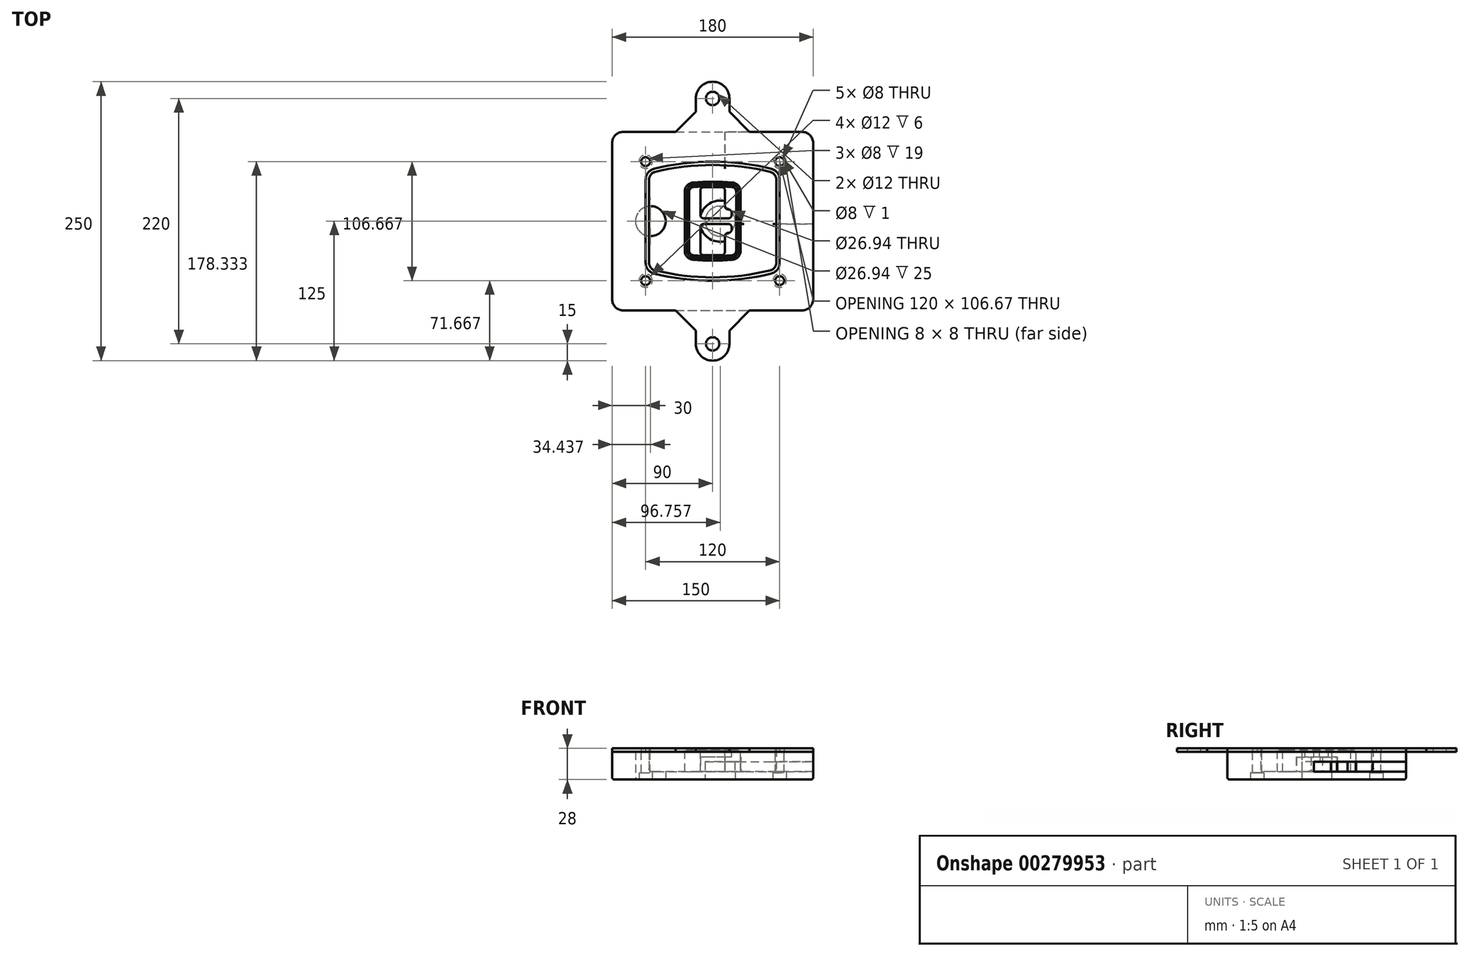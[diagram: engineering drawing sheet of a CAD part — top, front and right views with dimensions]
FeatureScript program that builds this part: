
annotation { "Feature Type Name" : "Feature", "Feature Type Description" : "" }
export const myFeature = defineFeature(function(context is Context, id is Id, definition is map)
    precondition{}
    {
        {
            var Q0;
            Q0=qCreatedBy(makeId("Top.planeOp"),FACE);
            var sketch = newSketch(context, id + "F0", { "sketchPlane" : qUnion([Q0])});
            skPoint(sketch, "E0.rect.middle", {"position": v(0, 0) * mm});
            skLineSegment(sketch, "E1.bottom", {"start": v(-80, -80) * mm, "end": v(80, -80) * mm});
            skLineSegment(sketch, "E1.top", {"start": v(-80, 80) * mm, "end": v(80, 80) * mm});
            skLineSegment(sketch, "E1.left", {"start": v(-90, -70) * mm, "end": v(-90, 70) * mm});
            skLineSegment(sketch, "E1.right", {"start": v(90, -70) * mm, "end": v(90, 70) * mm});
            skLineSegment(sketch, "E2", {"start": v(-90, 80) * mm, "end": v(90, -80) * mm, "construction": true});
            skLineSegment(sketch, "E3", {"start": v(90, 80) * mm, "end": v(-90, -80) * mm, "construction": true});
            skCircle(sketch, "E4", {"center": v(-60, 53.33) * mm, "radius": 4 * mm});
            skCircle(sketch, "E5", {"center": v(60, 53.33) * mm, "radius": 4 * mm});
            skCircle(sketch, "E6", {"center": v(60, -53.33) * mm, "radius": 4 * mm});
            skCircle(sketch, "E7", {"center": v(-60, -53.33) * mm, "radius": 4 * mm});
            skLineSegment(sketch, "E8", {"start": v(-60, 53.33) * mm, "end": v(60, 53.33) * mm, "construction": true});
            skLineSegment(sketch, "E9", {"start": v(60, 53.33) * mm, "end": v(60, -53.33) * mm, "construction": true});
            skLineSegment(sketch, "E10", {"start": v(60, -53.33) * mm, "end": v(-60, -53.33) * mm, "construction": true});
            skLineSegment(sketch, "E11", {"start": v(-60, -53.33) * mm, "end": v(-60, 53.33) * mm, "construction": true});
            skLineSegment(sketch, "E12", {"start": v(-60, 37.3) * mm, "end": v(-60, -37.3) * mm});
            skLineSegment(sketch, "E13", {"start": v(60, 37.3) * mm, "end": v(60, -37.3) * mm});
            skArc(sketch, "E14", {"start": v(52.38, 47.01) * mm, "mid": v(0, 53.33) * mm, "end": v(-52.38, 47.01) * mm});
            skArc(sketch, "E15", {"start": v(-52.38, -47.01) * mm, "mid": v(0, -53.33) * mm, "end": v(52.38, -47.01) * mm});
            skLineSegment(sketch, "E16", {"start": v(-60, 0) * mm, "end": v(60, 0) * mm, "construction": true});
            skPoint(sketch, "E17.visualSharp", {"position": v(-60, -45) * mm});
            skArc(sketch, "E17.filletArc", {"start": v(-60, -37.3) * mm, "mid": v(-57.87, -43.47) * mm, "end": v(-52.38, -47.01) * mm});
            skPoint(sketch, "E18.visualSharp", {"position": v(-60, 45) * mm});
            skArc(sketch, "E18.filletArc", {"start": v(-52.38, 47.01) * mm, "mid": v(-57.87, 43.47) * mm, "end": v(-60, 37.3) * mm});
            skPoint(sketch, "E19.visualSharp", {"position": v(60, 45) * mm});
            skArc(sketch, "E19.filletArc", {"start": v(60, 37.3) * mm, "mid": v(57.87, 43.47) * mm, "end": v(52.38, 47.01) * mm});
            skPoint(sketch, "E20.visualSharp", {"position": v(60, -45) * mm});
            skArc(sketch, "E20.filletArc", {"start": v(52.38, -47.01) * mm, "mid": v(57.87, -43.47) * mm, "end": v(60, -37.3) * mm});
            skPoint(sketch, "E21.visualSharp", {"position": v(-90, 80) * mm});
            skArc(sketch, "E21.filletArc", {"start": v(-80, 80) * mm, "mid": v(-87.07, 77.07) * mm, "end": v(-90, 70) * mm});
            skPoint(sketch, "E22.visualSharp", {"position": v(90, 80) * mm});
            skArc(sketch, "E22.filletArc", {"start": v(90, 70) * mm, "mid": v(87.07, 77.07) * mm, "end": v(80, 80) * mm});
            skPoint(sketch, "E23.visualSharp", {"position": v(90, -80) * mm});
            skArc(sketch, "E23.filletArc", {"start": v(80, -80) * mm, "mid": v(87.07, -77.07) * mm, "end": v(90, -70) * mm});
            skPoint(sketch, "E24.visualSharp", {"position": v(-90, -80) * mm});
            skArc(sketch, "E24.filletArc", {"start": v(-90, -70) * mm, "mid": v(-87.07, -77.07) * mm, "end": v(-80, -80) * mm});
            skArc(sketch, "E25.0", {"start": v(57, 37.3) * mm, "mid": v(55.5, 41.62) * mm, "end": v(51.67, 44.1) * mm});
            skLineSegment(sketch, "E25.1", {"start": v(57, 37.3) * mm, "end": v(57, -37.3) * mm});
            skArc(sketch, "E25.2", {"start": v(51.67, -44.1) * mm, "mid": v(55.5, -41.62) * mm, "end": v(57, -37.3) * mm});
            skArc(sketch, "E25.3", {"start": v(-51.67, -44.1) * mm, "mid": v(0, -50.33) * mm, "end": v(51.67, -44.1) * mm});
            skArc(sketch, "E25.4", {"start": v(-57, -37.3) * mm, "mid": v(-55.5, -41.62) * mm, "end": v(-51.67, -44.1) * mm});
            skArc(sketch, "E25.5", {"start": v(51.67, 44.1) * mm, "mid": v(0, 50.33) * mm, "end": v(-51.67, 44.1) * mm});
            skLineSegment(sketch, "E25.6", {"start": v(-57, 37.3) * mm, "end": v(-57, -37.3) * mm});
            skArc(sketch, "E25.7", {"start": v(-51.67, 44.1) * mm, "mid": v(-55.5, 41.62) * mm, "end": v(-57, 37.3) * mm});
            skArc(sketch, "E26.0", {"start": v(-53.33, 50.9) * mm, "mid": v(-61.01, 45.94) * mm, "end": v(-64, 37.3) * mm});
            skArc(sketch, "E26.1", {"start": v(53.33, 50.9) * mm, "mid": v(0, 57.33) * mm, "end": v(-53.33, 50.9) * mm});
            skArc(sketch, "E26.2", {"start": v(64, 37.3) * mm, "mid": v(61.01, 45.94) * mm, "end": v(53.33, 50.9) * mm});
            skLineSegment(sketch, "E26.3", {"start": v(64, 37.3) * mm, "end": v(64, -37.3) * mm});
            skArc(sketch, "E26.4", {"start": v(53.33, -50.9) * mm, "mid": v(61.01, -45.94) * mm, "end": v(64, -37.3) * mm});
            skLineSegment(sketch, "E26.5", {"start": v(-64, 37.3) * mm, "end": v(-64, -37.3) * mm});
            skArc(sketch, "E26.6", {"start": v(-53.33, -50.9) * mm, "mid": v(0, -57.33) * mm, "end": v(53.33, -50.9) * mm});
            skArc(sketch, "E26.7", {"start": v(-64, -37.3) * mm, "mid": v(-61.01, -45.94) * mm, "end": v(-53.33, -50.9) * mm});
            skSolve(sketch);
        }
        {
            var Q0;
            Q0=makeQuery(id+"F0.imprint","IMPRINT",FACE,{"disambiguationData":[TD([[makeQuery(id+"F0.imprint","IMPRINT",EDGE,{"derivedFrom":sQuery(id+"F0.wireOp",EDGE,"E1.bottom")}),1.0]])]});
            var Q1;
            Q1=makeQuery(id+"F0.imprint","IMPRINT",FACE,{"disambiguationData":[TD([[makeQuery(id+"F0.imprint","IMPRINT",EDGE,{"derivedFrom":sQuery(id+"F0.wireOp",EDGE,"E12")}),1.0]])]});
            var Q2;
            Q2=makeQuery(id+"F0.imprint","IMPRINT",FACE,{"disambiguationData":[TD([[makeQuery(id+"F0.imprint","IMPRINT",EDGE,{"derivedFrom":sQuery(id+"F0.wireOp",EDGE,"E25.0")}),1.0]])]});
            var Q3;
            Q3=makeQuery(id+"F0.imprint","IMPRINT",FACE,{"disambiguationData":[TD([[makeQuery(id+"F0.imprint","IMPRINT",EDGE,{"derivedFrom":sQuery(id+"F0.wireOp",EDGE,"E12")}),-1.0]])]});
            extrude(context, id + "F1", {"entities" : qUnion([Q0, Q1, Q2, Q3]), "oppositeDirection" : true, "depth" : 25 * mm});
        }
        {
            var Q0;
            Q0=makeQuery(id+"F0.imprint","IMPRINT",FACE,{"disambiguationData":[TD([[makeQuery(id+"F0.imprint","IMPRINT",EDGE,{"derivedFrom":sQuery(id+"F0.wireOp",EDGE,"E12")}),1.0]])]});
            extrude(context, id + "F2", {"entities" : qUnion([Q0]), "operationType" : NewBodyOperationType.ADD, "depth" : 3 * mm});
        }
        {
            var Q0;
            Q0=makeQuery(id+"F0.imprint","IMPRINT",FACE,{"disambiguationData":[TD([[makeQuery(id+"F0.imprint","IMPRINT",EDGE,{"derivedFrom":sQuery(id+"F0.wireOp",EDGE,"E25.0")}),1.0]])]});
            extrude(context, id + "F3", {"entities" : qUnion([Q0]), "operationType" : NewBodyOperationType.REMOVE, "oppositeDirection" : true, "depth" : 18 * mm});
        }
        {
            var Q0;
            Q0=makeQuery(id+"F2.opExtrude","CAP_FACE",FACE,{"disambiguationData":[OSD([sQuery(id+"F0.wireOp",EDGE,"E12"),sQuery(id+"F0.wireOp",EDGE,"E13"),sQuery(id+"F0.wireOp",EDGE,"E14"),sQuery(id+"F0.wireOp",EDGE,"E15"),sQuery(id+"F0.wireOp",EDGE,"E17.filletArc"),sQuery(id+"F0.wireOp",EDGE,"E18.filletArc"),sQuery(id+"F0.wireOp",EDGE,"E19.filletArc"),sQuery(id+"F0.wireOp",EDGE,"E20.filletArc"),sQuery(id+"F0.wireOp",EDGE,"E25.0"),sQuery(id+"F0.wireOp",EDGE,"E25.1"),sQuery(id+"F0.wireOp",EDGE,"E25.2"),sQuery(id+"F0.wireOp",EDGE,"E25.3"),sQuery(id+"F0.wireOp",EDGE,"E25.4"),sQuery(id+"F0.wireOp",EDGE,"E25.5"),sQuery(id+"F0.wireOp",EDGE,"E25.6"),sQuery(id+"F0.wireOp",EDGE,"E25.7")])],"isStart":false});
            var sketch = newSketch(context, id + "F4", { "sketchPlane" : qUnion([Q0])});
            skArc(sketch, "E27.0", {"start": v(-17.7, -34.56) * mm, "mid": v(0, -35.33) * mm, "end": v(17.7, -34.56) * mm});
            skArc(sketch, "E28.0", {"start": v(17.7, 34.56) * mm, "mid": v(0, 35.33) * mm, "end": v(-17.7, 34.56) * mm});
            skLineSegment(sketch, "E29", {"start": v(-25, 26.59) * mm, "end": v(-25, -26.59) * mm});
            skLineSegment(sketch, "E30", {"start": v(25, 26.59) * mm, "end": v(25, -26.59) * mm});
            skLineSegment(sketch, "E31", {"start": v(-25, 33.78) * mm, "end": v(25, 33.78) * mm, "construction": true});
            skLineSegment(sketch, "E32", {"start": v(-25, -33.78) * mm, "end": v(25, -33.78) * mm, "construction": true});
            skPoint(sketch, "E33.visualSharp", {"position": v(-25, 33.78) * mm});
            skArc(sketch, "E33.filletArc", {"start": v(-17.7, 34.56) * mm, "mid": v(-22.9, 32) * mm, "end": v(-25, 26.59) * mm});
            skPoint(sketch, "E34.visualSharp", {"position": v(25, 33.78) * mm});
            skArc(sketch, "E34.filletArc", {"start": v(25, 26.59) * mm, "mid": v(22.9, 32) * mm, "end": v(17.7, 34.56) * mm});
            skPoint(sketch, "E35.visualSharp", {"position": v(25, -33.78) * mm});
            skArc(sketch, "E35.filletArc", {"start": v(17.7, -34.56) * mm, "mid": v(22.9, -32) * mm, "end": v(25, -26.59) * mm});
            skPoint(sketch, "E36.visualSharp", {"position": v(-25, -33.78) * mm});
            skArc(sketch, "E36.filletArc", {"start": v(-25, -26.59) * mm, "mid": v(-22.9, -32) * mm, "end": v(-17.7, -34.56) * mm});
            skArc(sketch, "E37.0", {"start": v(51.67, 44.1) * mm, "mid": v(0, 50.33) * mm, "end": v(-51.67, 44.1) * mm});
            skArc(sketch, "E37.1", {"start": v(-51.67, 44.1) * mm, "mid": v(-55.5, 41.62) * mm, "end": v(-57, 37.3) * mm});
            skLineSegment(sketch, "E37.2", {"start": v(-57, 37.3) * mm, "end": v(-57, -37.3) * mm});
            skArc(sketch, "E37.3", {"start": v(-57, -37.3) * mm, "mid": v(-55.5, -41.62) * mm, "end": v(-51.67, -44.1) * mm});
            skArc(sketch, "E37.4", {"start": v(-51.67, -44.1) * mm, "mid": v(0, -50.33) * mm, "end": v(51.67, -44.1) * mm});
            skArc(sketch, "E37.5", {"start": v(51.67, -44.1) * mm, "mid": v(55.5, -41.62) * mm, "end": v(57, -37.3) * mm});
            skLineSegment(sketch, "E37.6", {"start": v(57, 37.3) * mm, "end": v(57, -37.3) * mm});
            skArc(sketch, "E37.7", {"start": v(57, 37.3) * mm, "mid": v(55.5, 41.62) * mm, "end": v(51.67, 44.1) * mm});
            skLineSegment(sketch, "E38.0", {"start": v(23, 26.59) * mm, "end": v(23, -26.59) * mm});
            skArc(sketch, "E38.1", {"start": v(17.53, -32.56) * mm, "mid": v(21.42, -30.64) * mm, "end": v(23, -26.59) * mm});
            skArc(sketch, "E38.2", {"start": v(-17.53, -32.56) * mm, "mid": v(0, -33.33) * mm, "end": v(17.53, -32.56) * mm});
            skArc(sketch, "E38.3", {"start": v(-23, -26.59) * mm, "mid": v(-21.42, -30.64) * mm, "end": v(-17.53, -32.56) * mm});
            skLineSegment(sketch, "E38.4", {"start": v(-23, 26.59) * mm, "end": v(-23, -26.59) * mm});
            skArc(sketch, "E38.5", {"start": v(23, 26.59) * mm, "mid": v(21.42, 30.64) * mm, "end": v(17.53, 32.56) * mm});
            skArc(sketch, "E38.6", {"start": v(-17.53, 32.56) * mm, "mid": v(-21.42, 30.64) * mm, "end": v(-23, 26.59) * mm});
            skArc(sketch, "E38.7", {"start": v(17.53, 32.56) * mm, "mid": v(0, 33.33) * mm, "end": v(-17.53, 32.56) * mm});
            skArc(sketch, "E39.0", {"start": v(21, 26.59) * mm, "mid": v(19.95, 29.29) * mm, "end": v(17.35, 30.57) * mm});
            skLineSegment(sketch, "E39.1", {"start": v(21, 26.59) * mm, "end": v(21, -26.59) * mm});
            skArc(sketch, "E39.2", {"start": v(17.35, -30.57) * mm, "mid": v(19.95, -29.29) * mm, "end": v(21, -26.59) * mm});
            skArc(sketch, "E39.3", {"start": v(-17.35, -30.57) * mm, "mid": v(0, -31.33) * mm, "end": v(17.35, -30.57) * mm});
            skArc(sketch, "E39.4", {"start": v(-21, -26.59) * mm, "mid": v(-19.95, -29.29) * mm, "end": v(-17.35, -30.57) * mm});
            skArc(sketch, "E39.5", {"start": v(17.35, 30.57) * mm, "mid": v(0, 31.33) * mm, "end": v(-17.35, 30.57) * mm});
            skLineSegment(sketch, "E39.6", {"start": v(-21, 26.59) * mm, "end": v(-21, -26.59) * mm});
            skArc(sketch, "E39.7", {"start": v(-17.35, 30.57) * mm, "mid": v(-19.95, 29.29) * mm, "end": v(-21, 26.59) * mm});
            skLineSegment(sketch, "E40", {"start": v(-25, 0) * mm, "end": v(25, 0) * mm, "construction": true});
            skLineSegment(sketch, "E41", {"start": v(-11, 5.5) * mm, "end": v(-11, 27.5) * mm});
            skLineSegment(sketch, "E42", {"start": v(-8, 30.5) * mm, "end": v(8, 30.5) * mm});
            skLineSegment(sketch, "E43", {"start": v(11, 27.5) * mm, "end": v(11, 13.5) * mm});
            skLineSegment(sketch, "E44", {"start": v(14, 10.5) * mm, "end": v(14, 10.5) * mm});
            skLineSegment(sketch, "E45", {"start": v(17, 7.5) * mm, "end": v(17, 5.5) * mm});
            skLineSegment(sketch, "E46", {"start": v(14, 2.5) * mm, "end": v(-8, 2.5) * mm});
            skPoint(sketch, "E47.visualSharp", {"position": v(-11, 30.5) * mm});
            skArc(sketch, "E47.filletArc", {"start": v(-8, 30.5) * mm, "mid": v(-10.12, 29.62) * mm, "end": v(-11, 27.5) * mm});
            skPoint(sketch, "E48.visualSharp", {"position": v(11, 30.5) * mm});
            skArc(sketch, "E48.filletArc", {"start": v(11, 27.5) * mm, "mid": v(10.12, 29.62) * mm, "end": v(8, 30.5) * mm});
            skPoint(sketch, "E49.visualSharp", {"position": v(11, 10.5) * mm});
            skArc(sketch, "E49.filletArc", {"start": v(11, 13.5) * mm, "mid": v(11.88, 11.38) * mm, "end": v(14, 10.5) * mm});
            skPoint(sketch, "E50.visualSharp", {"position": v(17, 10.5) * mm});
            skArc(sketch, "E50.filletArc", {"start": v(17, 7.5) * mm, "mid": v(16.12, 9.62) * mm, "end": v(14, 10.5) * mm});
            skPoint(sketch, "E51.visualSharp", {"position": v(17, 2.5) * mm});
            skArc(sketch, "E51.filletArc", {"start": v(14, 2.5) * mm, "mid": v(16.12, 3.38) * mm, "end": v(17, 5.5) * mm});
            skPoint(sketch, "E52.visualSharp", {"position": v(-11, 2.5) * mm});
            skArc(sketch, "E52.filletArc", {"start": v(-11, 5.5) * mm, "mid": v(-10.12, 3.38) * mm, "end": v(-8, 2.5) * mm});
            skLineSegment(sketch, "E53.0.MirrorCS", {"start": v(14, -2.5) * mm, "end": v(-8, -2.5) * mm});
            skArc(sketch, "E54.0.MirrorCS", {"start": v(-11, -5.5) * mm, "mid": v(-10.12, -3.38) * mm, "end": v(-8, -2.5) * mm});
            skLineSegment(sketch, "E55.0.MirrorCS", {"start": v(-11, -5.5) * mm, "end": v(-11, -27.5) * mm});
            skArc(sketch, "E56.0.MirrorCS", {"start": v(-8, -30.5) * mm, "mid": v(-10.12, -29.62) * mm, "end": v(-11, -27.5) * mm});
            skLineSegment(sketch, "E57.0.MirrorCS", {"start": v(-8, -30.5) * mm, "end": v(8, -30.5) * mm});
            skArc(sketch, "E58.0.MirrorCS", {"start": v(11, -27.5) * mm, "mid": v(10.12, -29.62) * mm, "end": v(8, -30.5) * mm});
            skLineSegment(sketch, "E59.0.MirrorCS", {"start": v(11, -27.5) * mm, "end": v(11, -13.5) * mm});
            skArc(sketch, "E60.0.MirrorCS", {"start": v(11, -13.5) * mm, "mid": v(11.88, -11.38) * mm, "end": v(14, -10.5) * mm});
            skArc(sketch, "E61.0.MirrorCS", {"start": v(17, -7.5) * mm, "mid": v(16.12, -9.62) * mm, "end": v(14, -10.5) * mm});
            skLineSegment(sketch, "E62.0.MirrorCS", {"start": v(17, -7.5) * mm, "end": v(17, -5.5) * mm});
            skArc(sketch, "E63.0.MirrorCS", {"start": v(14, -2.5) * mm, "mid": v(16.12, -3.38) * mm, "end": v(17, -5.5) * mm});
            skSolve(sketch);
        }
        {
            var Q0;
            Q0=makeQuery(id+"F4.imprint","IMPRINT",FACE,{"disambiguationData":[TD([[makeQuery(id+"F4.imprint","IMPRINT",EDGE,{"derivedFrom":sQuery(id+"F4.wireOp",EDGE,"E27.0")}),1.0]])]});
            var Q1;
            Q1=makeQuery(id+"F4.imprint","IMPRINT",FACE,{"disambiguationData":[TD([[makeQuery(id+"F4.imprint","IMPRINT",EDGE,{"derivedFrom":sQuery(id+"F4.wireOp",EDGE,"E38.0")}),-1.0]])]});
            var Q2;
            Q2=makeQuery(id+"F4.imprint","IMPRINT",FACE,{"disambiguationData":[TD([[makeQuery(id+"F4.imprint","IMPRINT",EDGE,{"derivedFrom":sQuery(id+"F4.wireOp",EDGE,"E39.0")}),1.0]])]});
            extrude(context, id + "F5", {"entities" : qUnion([Q0, Q1, Q2]), "operationType" : NewBodyOperationType.ADD, "endBound" : BoundingType.UP_TO_NEXT, "oppositeDirection" : true, "depth" : 25 * mm});
        }
        {
            var Q0;
            Q0=makeQuery(id+"F4.imprint","IMPRINT",FACE,{"disambiguationData":[TD([[makeQuery(id+"F4.imprint","IMPRINT",EDGE,{"derivedFrom":sQuery(id+"F4.wireOp",EDGE,"E38.0")}),-1.0]])]});
            extrude(context, id + "F6", {"entities" : qUnion([Q0]), "operationType" : NewBodyOperationType.REMOVE, "oppositeDirection" : true, "depth" : 2 * mm});
        }
        {
            var Q0;
            Q0=makeQuery(id+"F1.opExtrude","CAP_FACE",FACE,{"disambiguationData":[OSD([sQuery(id+"F0.wireOp",EDGE,"E1.bottom"),sQuery(id+"F0.wireOp",EDGE,"E1.top"),sQuery(id+"F0.wireOp",EDGE,"E1.left"),sQuery(id+"F0.wireOp",EDGE,"E1.right"),sQuery(id+"F0.wireOp",EDGE,"E4"),sQuery(id+"F0.wireOp",EDGE,"E5"),sQuery(id+"F0.wireOp",EDGE,"E6"),sQuery(id+"F0.wireOp",EDGE,"E7"),sQuery(id+"F0.wireOp",EDGE,"E21.filletArc"),sQuery(id+"F0.wireOp",EDGE,"E22.filletArc"),sQuery(id+"F0.wireOp",EDGE,"E23.filletArc"),sQuery(id+"F0.wireOp",EDGE,"E24.filletArc")])],"isStart":false});
            var sketch = newSketch(context, id + "F7", { "sketchPlane" : qUnion([Q0])});
            skCircle(sketch, "E64", {"center": v(6.76, 0) * mm, "radius": 13.47 * mm});
            skCircle(sketch, "E65", {"center": v(-55.56, 0) * mm, "radius": 13.47 * mm});
            skLineSegment(sketch, "E66", {"start": v(90, 0) * mm, "end": v(-90, 0) * mm});
            skCircle(sketch, "E67", {"center": v(6.76, 0) * mm, "radius": 18.47 * mm});
            skCircle(sketch, "E68", {"center": v(60, -53.33) * mm, "radius": 6 * mm});
            skCircle(sketch, "E69", {"center": v(-60, -53.33) * mm, "radius": 6 * mm});
            skCircle(sketch, "E70", {"center": v(-60, 53.33) * mm, "radius": 6 * mm});
            skCircle(sketch, "E71", {"center": v(60, 53.33) * mm, "radius": 6 * mm});
            skSolve(sketch);
        }
        {
            var Q0;
            {var subQ1=sQuery(id+"F7.wireOp",EDGE,"E66");var subQ4=sQuery(id+"F7.wireOp",EDGE,"E64");var subQ6=makeQuery(id+"F7.imprint","INTERSECT",VERTEX,{"disambiguationData":[OD(0.0)],"derivedFrom":[subQ4,subQ1]});Q0=makeQuery(id+"F7.imprint","IMPRINT",FACE,{"disambiguationData":[TD([[makeQuery(id+"F7.imprint","IMPRINT",EDGE,{"disambiguationData":[TD([[subQ6,-1.0]])],"derivedFrom":subQ4}),-1.0]])]});}
            var Q1;
            {var subQ0=sQuery(id+"F7.wireOp",EDGE,"E66");var subQ1=sQuery(id+"F7.wireOp",EDGE,"E64");var subQ3=makeQuery(id+"F7.imprint","INTERSECT",VERTEX,{"disambiguationData":[OD(0.0)],"derivedFrom":[subQ1,subQ0]});Q1=makeQuery(id+"F7.imprint","IMPRINT",FACE,{"disambiguationData":[TD([[makeQuery(id+"F7.imprint","IMPRINT",EDGE,{"disambiguationData":[TD([[subQ3,-1.0]])],"derivedFrom":subQ1}),1.0]])]});}
            var Q2;
            {var subQ0=sQuery(id+"F7.wireOp",EDGE,"E66");var subQ1=sQuery(id+"F7.wireOp",EDGE,"E64");var subQ3=makeQuery(id+"F7.imprint","INTERSECT",VERTEX,{"disambiguationData":[OD(0.0)],"derivedFrom":[subQ1,subQ0]});Q2=makeQuery(id+"F7.imprint","IMPRINT",FACE,{"disambiguationData":[TD([[makeQuery(id+"F7.imprint","IMPRINT",EDGE,{"disambiguationData":[TD([[subQ3,1.0]])],"derivedFrom":subQ1}),1.0]])]});}
            var Q3;
            {var subQ1=sQuery(id+"F7.wireOp",EDGE,"E66");var subQ4=sQuery(id+"F7.wireOp",EDGE,"E64");var subQ6=makeQuery(id+"F7.imprint","INTERSECT",VERTEX,{"disambiguationData":[OD(0.0)],"derivedFrom":[subQ4,subQ1]});Q3=makeQuery(id+"F7.imprint","IMPRINT",FACE,{"disambiguationData":[TD([[makeQuery(id+"F7.imprint","IMPRINT",EDGE,{"disambiguationData":[TD([[subQ6,1.0]])],"derivedFrom":subQ4}),-1.0]])]});}
            extrude(context, id + "F8", {"entities" : qUnion([Q0, Q1, Q2, Q3]), "operationType" : NewBodyOperationType.ADD, "oppositeDirection" : true, "depth" : 20 * mm});
        }
        {
            var Q0;
            {var subQ0=sQuery(id+"F7.wireOp",EDGE,"E66");var subQ1=sQuery(id+"F7.wireOp",EDGE,"E64");var subQ3=makeQuery(id+"F7.imprint","INTERSECT",VERTEX,{"disambiguationData":[OD(0.0)],"derivedFrom":[subQ1,subQ0]});Q0=makeQuery(id+"F7.imprint","IMPRINT",FACE,{"disambiguationData":[TD([[makeQuery(id+"F7.imprint","IMPRINT",EDGE,{"disambiguationData":[TD([[subQ3,-1.0]])],"derivedFrom":subQ1}),1.0]])]});}
            var Q1;
            {var subQ0=sQuery(id+"F7.wireOp",EDGE,"E66");var subQ1=sQuery(id+"F7.wireOp",EDGE,"E64");var subQ3=makeQuery(id+"F7.imprint","INTERSECT",VERTEX,{"disambiguationData":[OD(0.0)],"derivedFrom":[subQ1,subQ0]});Q1=makeQuery(id+"F7.imprint","IMPRINT",FACE,{"disambiguationData":[TD([[makeQuery(id+"F7.imprint","IMPRINT",EDGE,{"disambiguationData":[TD([[subQ3,1.0]])],"derivedFrom":subQ1}),1.0]])]});}
            extrude(context, id + "F9", {"entities" : qUnion([Q0, Q1]), "operationType" : NewBodyOperationType.REMOVE, "oppositeDirection" : true, "depth" : 16 * mm});
        }
        {
            var Q0;
            {var subQ0=sQuery(id+"F7.wireOp",EDGE,"E66");var subQ1=sQuery(id+"F7.wireOp",EDGE,"E65");var subQ3=makeQuery(id+"F7.imprint","INTERSECT",VERTEX,{"disambiguationData":[OD(0.0)],"derivedFrom":[subQ1,subQ0]});Q0=makeQuery(id+"F7.imprint","IMPRINT",FACE,{"disambiguationData":[TD([[makeQuery(id+"F7.imprint","IMPRINT",EDGE,{"disambiguationData":[TD([[subQ3,-1.0]])],"derivedFrom":subQ1}),1.0]])]});}
            var Q1;
            {var subQ0=sQuery(id+"F7.wireOp",EDGE,"E66");var subQ1=sQuery(id+"F7.wireOp",EDGE,"E65");var subQ3=makeQuery(id+"F7.imprint","INTERSECT",VERTEX,{"disambiguationData":[OD(0.0)],"derivedFrom":[subQ1,subQ0]});Q1=makeQuery(id+"F7.imprint","IMPRINT",FACE,{"disambiguationData":[TD([[makeQuery(id+"F7.imprint","IMPRINT",EDGE,{"disambiguationData":[TD([[subQ3,1.0]])],"derivedFrom":subQ1}),1.0]])]});}
            extrude(context, id + "F10", {"entities" : qUnion([Q0, Q1]), "operationType" : NewBodyOperationType.REMOVE, "oppositeDirection" : true, "depth" : 25 * mm});
        }
        {
            var Q0;
            Q0=makeQuery(id+"F7.imprint","IMPRINT",FACE,{"disambiguationData":[TD([[makeQuery(id+"F7.imprint","IMPRINT",EDGE,{"derivedFrom":sQuery(id+"F7.wireOp",EDGE,"E68")}),1.0]])]});
            var Q1;
            Q1=makeQuery(id+"F7.imprint","IMPRINT",FACE,{"disambiguationData":[TD([[makeQuery(id+"F7.imprint","IMPRINT",EDGE,{"derivedFrom":makeQuery(id+"F1.opExtrude","CAP_EDGE",EDGE,{"disambiguationData":[OSD([sQuery(id+"F0.wireOp",EDGE,"E5")])],"isStart":false})}),-1.0]])]});
            var Q2;
            Q2=makeQuery(id+"F7.imprint","IMPRINT",FACE,{"disambiguationData":[TD([[makeQuery(id+"F7.imprint","IMPRINT",EDGE,{"derivedFrom":sQuery(id+"F7.wireOp",EDGE,"E69")}),1.0]])]});
            var Q3;
            Q3=makeQuery(id+"F7.imprint","IMPRINT",FACE,{"disambiguationData":[TD([[makeQuery(id+"F7.imprint","IMPRINT",EDGE,{"derivedFrom":makeQuery(id+"F1.opExtrude","CAP_EDGE",EDGE,{"disambiguationData":[OSD([sQuery(id+"F0.wireOp",EDGE,"E4")])],"isStart":false})}),-1.0]])]});
            var Q4;
            Q4=makeQuery(id+"F7.imprint","IMPRINT",FACE,{"disambiguationData":[TD([[makeQuery(id+"F7.imprint","IMPRINT",EDGE,{"derivedFrom":sQuery(id+"F7.wireOp",EDGE,"E70")}),1.0]])]});
            var Q5;
            Q5=makeQuery(id+"F7.imprint","IMPRINT",FACE,{"disambiguationData":[TD([[makeQuery(id+"F7.imprint","IMPRINT",EDGE,{"derivedFrom":makeQuery(id+"F1.opExtrude","CAP_EDGE",EDGE,{"disambiguationData":[OSD([sQuery(id+"F0.wireOp",EDGE,"E7")])],"isStart":false})}),-1.0]])]});
            var Q6;
            Q6=makeQuery(id+"F7.imprint","IMPRINT",FACE,{"disambiguationData":[TD([[makeQuery(id+"F7.imprint","IMPRINT",EDGE,{"derivedFrom":sQuery(id+"F7.wireOp",EDGE,"E71")}),1.0]])]});
            var Q7;
            Q7=makeQuery(id+"F7.imprint","IMPRINT",FACE,{"disambiguationData":[TD([[makeQuery(id+"F7.imprint","IMPRINT",EDGE,{"derivedFrom":makeQuery(id+"F1.opExtrude","CAP_EDGE",EDGE,{"disambiguationData":[OSD([sQuery(id+"F0.wireOp",EDGE,"E6")])],"isStart":false})}),-1.0]])]});
            extrude(context, id + "F11", {"entities" : qUnion([Q0, Q1, Q2, Q3, Q4, Q5, Q6, Q7]), "operationType" : NewBodyOperationType.REMOVE, "oppositeDirection" : true, "depth" : 6 * mm});
        }
        {
            var Q0;
            Q0=makeQuery(id+"F9.boolean.opBoolean","COPY",FACE,{"derivedFrom":makeQuery(id+"F9.opExtrude","CAP_FACE",FACE,{"disambiguationData":[OSD([sQuery(id+"F7.wireOp",EDGE,"E64")])],"isStart":false})});
            var sketch = newSketch(context, id + "F12", { "sketchPlane" : qUnion([Q0])});
            skArc(sketch, "E72.0", {"start": v(11, -88.19) * mm, "mid": v(97.1, -83.6) * mm, "end": v(92.5, 2.5) * mm});
            skLineSegment(sketch, "E72.1", {"start": v(11, -17.97) * mm, "end": v(11, -17.97) * mm});
            skLineSegment(sketch, "E73", {"start": v(92.5, -105.13) * mm, "end": v(102.3, -105.13) * mm});
            skLineSegment(sketch, "E74.0", {"start": v(92.5, 2.5) * mm, "end": v(14, 2.5) * mm});
            skArc(sketch, "E74.1", {"start": v(14, 2.5) * mm, "mid": v(16.12, 3.38) * mm, "end": v(17, 5.5) * mm});
            skLineSegment(sketch, "E74.2", {"start": v(17, 7.5) * mm, "end": v(17, 5.5) * mm});
            skArc(sketch, "E74.3", {"start": v(17, 7.5) * mm, "mid": v(16.12, 9.62) * mm, "end": v(14, 10.5) * mm});
            skArc(sketch, "E74.4", {"start": v(11, 13.5) * mm, "mid": v(11.88, 11.38) * mm, "end": v(14, 10.5) * mm});
            skLineSegment(sketch, "E74.5", {"start": v(11, 13.5) * mm, "end": v(11, -88.19) * mm});
            skLineSegment(sketch, "E74.7", {"start": v(92.5, -2.5) * mm, "end": v(14, -2.5) * mm});
            skArc(sketch, "E74.8", {"start": v(14, -2.5) * mm, "mid": v(16.12, -3.38) * mm, "end": v(17, -5.5) * mm});
            skLineSegment(sketch, "E74.9", {"start": v(17, -7.5) * mm, "end": v(17, -5.5) * mm});
            skArc(sketch, "E74.10", {"start": v(17, -7.5) * mm, "mid": v(16.12, -9.62) * mm, "end": v(14, -10.5) * mm});
            skArc(sketch, "E74.11", {"start": v(11, -13.5) * mm, "mid": v(11.88, -11.38) * mm, "end": v(14, -10.5) * mm});
            skLineSegment(sketch, "E74.12", {"start": v(11, -17.97) * mm, "end": v(11, -13.5) * mm});
            skPoint(sketch, "E75.orphan", {"position": v(11, -27.5) * mm});
            skPoint(sketch, "E76.orphan", {"position": v(-8, -2.5) * mm});
            skPoint(sketch, "E77.orphan", {"position": v(-8, 2.5) * mm});
            skPoint(sketch, "E78.orphan", {"position": v(11, 27.5) * mm});
            skSolve(sketch);
        }
        {
            var Q0;
            {var subQ7=sQuery(id+"F12.wireOp",EDGE,"E72.0");var subQ14=sQuery(id+"F12.wireOp",EDGE,"E72.1");var subQ16=sQuery(id+"F12.wireOp",EDGE,"E74.1");var subQ18=sQuery(id+"F12.wireOp",EDGE,"E74.8");Q0=qUnion([makeQuery(id+"F12.imprint","IMPRINT",FACE,{"disambiguationData":[TD([[makeQuery(id+"F12.imprint","IMPRINT",EDGE,{"derivedFrom":subQ7}),1.0]])]}),makeQuery(id+"F12.imprint","IMPRINT",FACE,{"disambiguationData":[TD([[makeQuery(id+"F12.imprint","IMPRINT",EDGE,{"derivedFrom":subQ14}),1.0]])]}),makeQuery(id+"F12.imprint","IMPRINT",FACE,{"disambiguationData":[TD([[makeQuery(id+"F12.imprint","IMPRINT",EDGE,{"derivedFrom":subQ16}),1.0]])]}),makeQuery(id+"F12.imprint","IMPRINT",FACE,{"disambiguationData":[TD([[makeQuery(id+"F12.imprint","IMPRINT",EDGE,{"derivedFrom":subQ18}),-1.0]])]})]);}
            var Q1;
            Q1=makeQuery(id+"F5.boolean.opBoolean","SPLIT",FACE,{"disambiguationData":[TD([makeQuery(id+"F5.opExtrude","SWEPT_FACE",FACE,{"disambiguationData":[OSD([sQuery(id+"F4.wireOp",EDGE,"E41")])]})])],"derivedFrom":makeQuery(id+"F3.boolean.opBoolean","COPY",FACE,{"derivedFrom":makeQuery(id+"F3.opExtrude","CAP_FACE",FACE,{"disambiguationData":[OSD([sQuery(id+"F0.wireOp",EDGE,"E25.0"),sQuery(id+"F0.wireOp",EDGE,"E25.1"),sQuery(id+"F0.wireOp",EDGE,"E25.2"),sQuery(id+"F0.wireOp",EDGE,"E25.3"),sQuery(id+"F0.wireOp",EDGE,"E25.4"),sQuery(id+"F0.wireOp",EDGE,"E25.5"),sQuery(id+"F0.wireOp",EDGE,"E25.6"),sQuery(id+"F0.wireOp",EDGE,"E25.7")])],"isStart":false})})});
            extrude(context, id + "F13", {"entities" : qUnion([Q0]), "operationType" : NewBodyOperationType.REMOVE, "endBound" : BoundingType.UP_TO_SURFACE, "endBoundEntityFace" : qUnion([Q1]), "depth" : 25 * mm});
        }
        {
            var Q0;
            Q0=makeQuery(id+"F3.boolean.opBoolean","COPY",EDGE,{"derivedFrom":makeQuery(id+"F3.opExtrude","CAP_EDGE",EDGE,{"disambiguationData":[OSD([sQuery(id+"F0.wireOp",EDGE,"E25.6")])],"isStart":false})});
            var Q1;
            Q1=makeQuery(id+"F8.boolean.opBoolean","INTERSECT",EDGE,{"derivedFrom":[makeQuery(id+"F5.opExtrude","SWEPT_FACE",FACE,{"disambiguationData":[OSD([sQuery(id+"F4.wireOp",EDGE,"E30")])]}),makeQuery(id+"F8.opExtrude","CAP_FACE",FACE,{"disambiguationData":[OSD([sQuery(id+"F7.wireOp",EDGE,"E67")])],"isStart":false})]});
            var Q2;
            Q2=makeQuery(id+"F8.boolean.opBoolean","INTERSECT",EDGE,{"disambiguationData":[OD(1.0)],"derivedFrom":[makeQuery(id+"F5.opExtrude","SWEPT_FACE",FACE,{"disambiguationData":[OSD([sQuery(id+"F4.wireOp",EDGE,"E30")])]}),makeQuery(id+"F8.opExtrude","SWEPT_FACE",FACE,{"disambiguationData":[OSD([sQuery(id+"F7.wireOp",EDGE,"E67")])]})]});
            var Q3;
            {var subQ0=makeQuery(id+"F3.boolean.opBoolean","COPY",FACE,{"derivedFrom":makeQuery(id+"F3.opExtrude","CAP_FACE",FACE,{"disambiguationData":[OSD([sQuery(id+"F0.wireOp",EDGE,"E25.0"),sQuery(id+"F0.wireOp",EDGE,"E25.1"),sQuery(id+"F0.wireOp",EDGE,"E25.2"),sQuery(id+"F0.wireOp",EDGE,"E25.3"),sQuery(id+"F0.wireOp",EDGE,"E25.4"),sQuery(id+"F0.wireOp",EDGE,"E25.5"),sQuery(id+"F0.wireOp",EDGE,"E25.6"),sQuery(id+"F0.wireOp",EDGE,"E25.7")])],"isStart":false})});var subQ1=sQuery(id+"F4.wireOp",EDGE,"E30");Q3=makeQuery(id+"F8.boolean.opBoolean","SPLIT",EDGE,{"disambiguationData":[TD([makeQuery(id+"F5.opExtrude","SWEPT_FACE",FACE,{"disambiguationData":[OSD([sQuery(id+"F4.wireOp",EDGE,"E35.filletArc")])]})])],"derivedFrom":makeQuery(id+"F5.opExtrude","TWEAK_EDGE",EDGE,{"derivedFrom":[subQ0,makeQuery(id+"F4.imprint","IMPRINT",EDGE,{"derivedFrom":subQ1})]})});}
            var Q4;
            {var subQ0=sQuery(id+"F0.wireOp",EDGE,"E25.0");var subQ1=sQuery(id+"F0.wireOp",EDGE,"E25.1");var subQ2=sQuery(id+"F0.wireOp",EDGE,"E25.2");var subQ3=sQuery(id+"F0.wireOp",EDGE,"E25.3");var subQ4=sQuery(id+"F0.wireOp",EDGE,"E25.4");var subQ5=sQuery(id+"F0.wireOp",EDGE,"E25.5");var subQ6=sQuery(id+"F0.wireOp",EDGE,"E25.6");var subQ7=sQuery(id+"F0.wireOp",EDGE,"E25.7");Q4=makeQuery(id+"F8.boolean.opBoolean","INTERSECT",EDGE,{"derivedFrom":[makeQuery(id+"F5.boolean.opBoolean","SPLIT",FACE,{"disambiguationData":[TD([makeQuery(id+"F2.opExtrude","SWEPT_FACE",FACE,{"disambiguationData":[OSD([subQ0])]})])],"derivedFrom":makeQuery(id+"F3.boolean.opBoolean","COPY",FACE,{"derivedFrom":makeQuery(id+"F3.opExtrude","CAP_FACE",FACE,{"disambiguationData":[OSD([subQ0,subQ1,subQ2,subQ3,subQ4,subQ5,subQ6,subQ7])],"isStart":false})})}),makeQuery(id+"F8.opExtrude","SWEPT_FACE",FACE,{"disambiguationData":[OSD([sQuery(id+"F7.wireOp",EDGE,"E67")])]})]});}
            var Q5;
            Q5=makeQuery(id+"F8.boolean.opBoolean","INTERSECT",EDGE,{"disambiguationData":[OD(0.0)],"derivedFrom":[makeQuery(id+"F5.opExtrude","SWEPT_FACE",FACE,{"disambiguationData":[OSD([sQuery(id+"F4.wireOp",EDGE,"E30")])]}),makeQuery(id+"F8.opExtrude","SWEPT_FACE",FACE,{"disambiguationData":[OSD([sQuery(id+"F7.wireOp",EDGE,"E67")])]})]});
            fillet(context, id + "F14", {"entities" : qUnion([Q0, Q1, Q2, Q3, Q4, Q5]), "radius" : 3 * mm, "tangentPropagation" : true, "allowEdgeOverflow" : false});
        }
        {
            var Q0;
            Q0=makeQuery(id+"F1.opExtrude","CAP_EDGE",EDGE,{"disambiguationData":[OSD([sQuery(id+"F0.wireOp",EDGE,"E1.bottom")])],"isStart":false});
            fillet(context, id + "F15", {"entities" : qUnion([Q0]), "radius" : 2 * mm, "tangentPropagation" : true, "allowEdgeOverflow" : false});
        }
        {
            var Q0;
            {var subQ0=sQuery(id+"F0.wireOp",EDGE,"E22.filletArc");var subQ1=sQuery(id+"F0.wireOp",EDGE,"E7");var subQ2=sQuery(id+"F0.wireOp",EDGE,"E6");var subQ3=sQuery(id+"F0.wireOp",EDGE,"E5");var subQ4=sQuery(id+"F0.wireOp",EDGE,"E4");var subQ5=sQuery(id+"F0.wireOp",EDGE,"E1.bottom");var subQ6=sQuery(id+"F0.wireOp",EDGE,"E21.filletArc");var subQ7=sQuery(id+"F0.wireOp",EDGE,"E1.top");var subQ8=sQuery(id+"F0.wireOp",EDGE,"E1.left");var subQ9=sQuery(id+"F0.wireOp",EDGE,"E1.right");var subQ10=sQuery(id+"F0.wireOp",EDGE,"E23.filletArc");var subQ11=sQuery(id+"F0.wireOp",EDGE,"E24.filletArc");Q0=makeQuery(id+"F2.boolean.opBoolean","SPLIT",FACE,{"disambiguationData":[TD([makeQuery(id+"F1.opExtrude","SWEPT_FACE",FACE,{"disambiguationData":[OSD([subQ5])]})])],"derivedFrom":makeQuery(id+"F1.opExtrude","CAP_FACE",FACE,{"disambiguationData":[OSD([subQ5,subQ7,subQ8,subQ9,subQ4,subQ3,subQ2,subQ1,subQ6,subQ0,subQ10,subQ11])],"isStart":true})});}
            var sketch = newSketch(context, id + "F16", { "sketchPlane" : qUnion([Q0])});
            skCircle(sketch, "E79.0", {"center": v(-60, 53.33) * mm, "radius": 4 * mm});
            skLineSegment(sketch, "E79.1", {"start": v(-80, 80) * mm, "end": v(80, 80) * mm});
            skArc(sketch, "E79.2", {"start": v(-80, 80) * mm, "mid": v(-87.07, 77.07) * mm, "end": v(-90, 70) * mm});
            skLineSegment(sketch, "E79.3", {"start": v(-90, -70) * mm, "end": v(-90, 70) * mm});
            skArc(sketch, "E79.4", {"start": v(90, 70) * mm, "mid": v(87.07, 77.07) * mm, "end": v(80, 80) * mm});
            skLineSegment(sketch, "E79.5", {"start": v(90, -70) * mm, "end": v(90, 70) * mm});
            skLineSegment(sketch, "E79.6", {"start": v(-80, -80) * mm, "end": v(80, -80) * mm});
            skArc(sketch, "E79.7", {"start": v(80, -80) * mm, "mid": v(87.07, -77.07) * mm, "end": v(90, -70) * mm});
            skArc(sketch, "E79.8", {"start": v(-90, -70) * mm, "mid": v(-87.07, -77.07) * mm, "end": v(-80, -80) * mm});
            skCircle(sketch, "E79.9", {"center": v(60, 53.33) * mm, "radius": 4 * mm});
            skCircle(sketch, "E79.10", {"center": v(60, -53.33) * mm, "radius": 4 * mm});
            skCircle(sketch, "E79.11", {"center": v(-60, -53.33) * mm, "radius": 4 * mm});
            skArc(sketch, "E79.12", {"start": v(-52.38, -47.01) * mm, "mid": v(0, -53.33) * mm, "end": v(52.38, -47.01) * mm});
            skArc(sketch, "E79.13", {"start": v(-60, -37.3) * mm, "mid": v(-57.87, -43.47) * mm, "end": v(-52.38, -47.01) * mm});
            skLineSegment(sketch, "E79.14", {"start": v(-60, 37.3) * mm, "end": v(-60, -37.3) * mm});
            skArc(sketch, "E79.15", {"start": v(52.38, 47.01) * mm, "mid": v(0, 53.33) * mm, "end": v(-52.38, 47.01) * mm});
            skArc(sketch, "E79.16", {"start": v(-52.38, 47.01) * mm, "mid": v(-57.87, 43.47) * mm, "end": v(-60, 37.3) * mm});
            skLineSegment(sketch, "E79.17", {"start": v(60, 37.3) * mm, "end": v(60, -37.3) * mm});
            skArc(sketch, "E79.18", {"start": v(60, 37.3) * mm, "mid": v(57.87, 43.47) * mm, "end": v(52.38, 47.01) * mm});
            skArc(sketch, "E79.19", {"start": v(52.38, -47.01) * mm, "mid": v(57.87, -43.47) * mm, "end": v(60, -37.3) * mm});
            skPoint(sketch, "E79.20", {"position": v(60, 0) * mm});
            skLineSegment(sketch, "E80", {"start": v(0, 80) * mm, "end": v(0, 110) * mm, "construction": true});
            skPoint(sketch, "E80.endSnap0", {"position": v(0, 80) * mm});
            skCircle(sketch, "E81", {"center": v(0, 110) * mm, "radius": 6 * mm});
            skLineSegment(sketch, "E82", {"start": v(-15, 98) * mm, "end": v(-15, 110) * mm});
            skLineSegment(sketch, "E83", {"start": v(15, 98) * mm, "end": v(15, 110) * mm});
            skArc(sketch, "E84", {"start": v(15, 110) * mm, "mid": v(0, 125) * mm, "end": v(-15, 110) * mm});
            skLineSegment(sketch, "E85", {"start": v(-90, 0) * mm, "end": v(90, 0) * mm, "construction": true});
            skLineSegment(sketch, "E86", {"start": v(-15, 98) * mm, "end": v(-33, 80) * mm});
            skLineSegment(sketch, "E87", {"start": v(15, 98) * mm, "end": v(33, 80) * mm});
            skLineSegment(sketch, "E88.MirrorCS", {"start": v(-15, -98) * mm, "end": v(-33, -80) * mm});
            skArc(sketch, "E89.MirrorCS", {"start": v(15, -110) * mm, "mid": v(0, -125) * mm, "end": v(-15, -110) * mm});
            skCircle(sketch, "E90.MirrorC", {"center": v(0, -110) * mm, "radius": 6 * mm});
            skLineSegment(sketch, "E91.MirrorCS", {"start": v(0, -80) * mm, "end": v(0, -110) * mm, "construction": true});
            skLineSegment(sketch, "E92.MirrorCS", {"start": v(15, -98) * mm, "end": v(15, -110) * mm});
            skLineSegment(sketch, "E93.MirrorCS", {"start": v(15, -98) * mm, "end": v(33, -80) * mm});
            skLineSegment(sketch, "E94.MirrorCS", {"start": v(-15, -98) * mm, "end": v(-15, -110) * mm});
            skSolve(sketch);
        }
        {
            var Q0;
            Q0 = qSketchRegion(id + "F16", true);
            var Q1;
            Q1=makeQuery(id+"F2.opExtrude","CAP_FACE",FACE,{"disambiguationData":[OSD([sQuery(id+"F0.wireOp",EDGE,"E12"),sQuery(id+"F0.wireOp",EDGE,"E13"),sQuery(id+"F0.wireOp",EDGE,"E14"),sQuery(id+"F0.wireOp",EDGE,"E15"),sQuery(id+"F0.wireOp",EDGE,"E17.filletArc"),sQuery(id+"F0.wireOp",EDGE,"E18.filletArc"),sQuery(id+"F0.wireOp",EDGE,"E19.filletArc"),sQuery(id+"F0.wireOp",EDGE,"E20.filletArc"),sQuery(id+"F0.wireOp",EDGE,"E25.0"),sQuery(id+"F0.wireOp",EDGE,"E25.1"),sQuery(id+"F0.wireOp",EDGE,"E25.2"),sQuery(id+"F0.wireOp",EDGE,"E25.3"),sQuery(id+"F0.wireOp",EDGE,"E25.4"),sQuery(id+"F0.wireOp",EDGE,"E25.5"),sQuery(id+"F0.wireOp",EDGE,"E25.6"),sQuery(id+"F0.wireOp",EDGE,"E25.7")])],"isStart":false});
            extrude(context, id + "F17", {"entities" : qUnion([Q0]), "endBound" : BoundingType.UP_TO_SURFACE, "endBoundEntityFace" : qUnion([Q1]), "depth" : 25 * mm});
        }
    });
